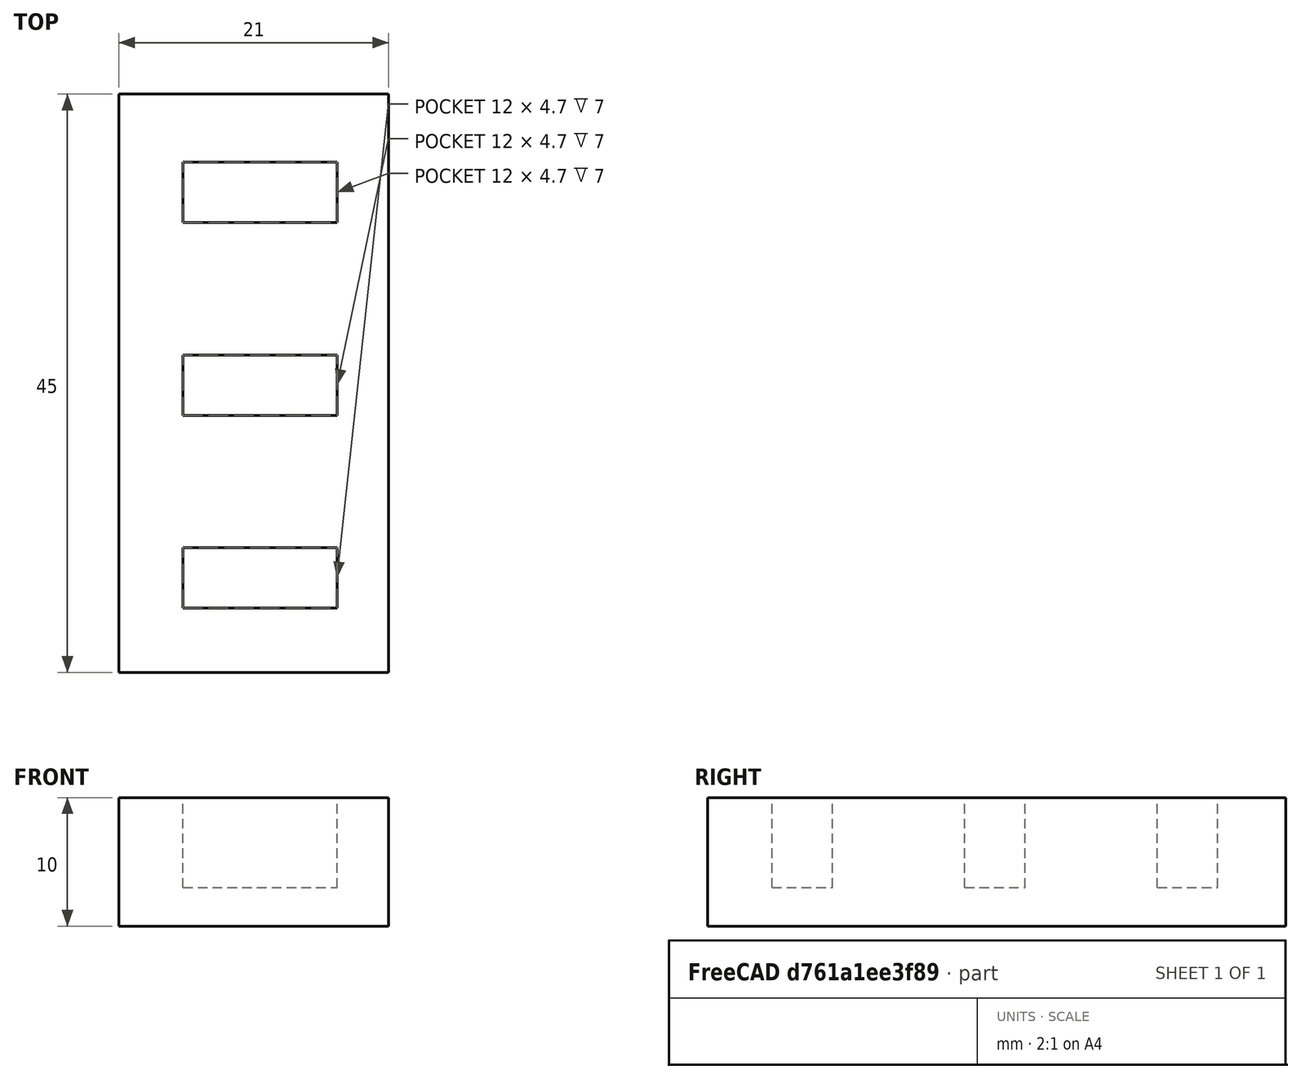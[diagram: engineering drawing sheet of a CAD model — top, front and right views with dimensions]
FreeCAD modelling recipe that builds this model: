
FCSTD DOCUMENT  (FreeCAD 0.21R33694 (Git))
Label: OJT1_T08P01_pendrives
License: All rights reserved
LicenseURL: https://en.wikipedia.org/wiki/All_rights_reserved
objects: Part::Box×4, Part::MultiFuse×1, Part::Cut×1
note: 6 computed .brp shape members not serialized (recipe doc carries the construction recipe); baked Part::Feature solids carry a one-line shape summary decoded from their .brp

FEATURE [Part::Box] Box  label="Ranura_1"
  AttacherType = Attacher::AttachEngine3D
  Height = 11
  Length = 12
  Width = 4.7
FEATURE [Part::Box] Box001  label="Ranura_2"
  AttacherType = Attacher::AttachEngine3D
  Height = 11
  Length = 12
  Placement = pos=(0,15,0) rot=(0,0,1;0rad)
  Width = 4.7
FEATURE [Part::Box] Box002  label="Ranura_3"
  AttacherType = Attacher::AttachEngine3D
  Height = 11
  Length = 12
  Placement = pos=(0,30,0) rot=(0,0,1;0rad)
  Width = 4.7
FEATURE [Part::MultiFuse] Fusion  label="Ranuras"
  Placement = pos=(5,5,3) rot=(0,0,1;0rad)
  Shapes = -> [Box,Box001,Box002]
FEATURE [Part::Box] Box003  label="Base"
  AttacherType = Attacher::AttachEngine3D
  Height = 10
  Length = 21
  Width = 45
FEATURE [Part::Cut] Cut  label="Porta-pendrives"
  Base = -> Box003
  Tool = -> Fusion
